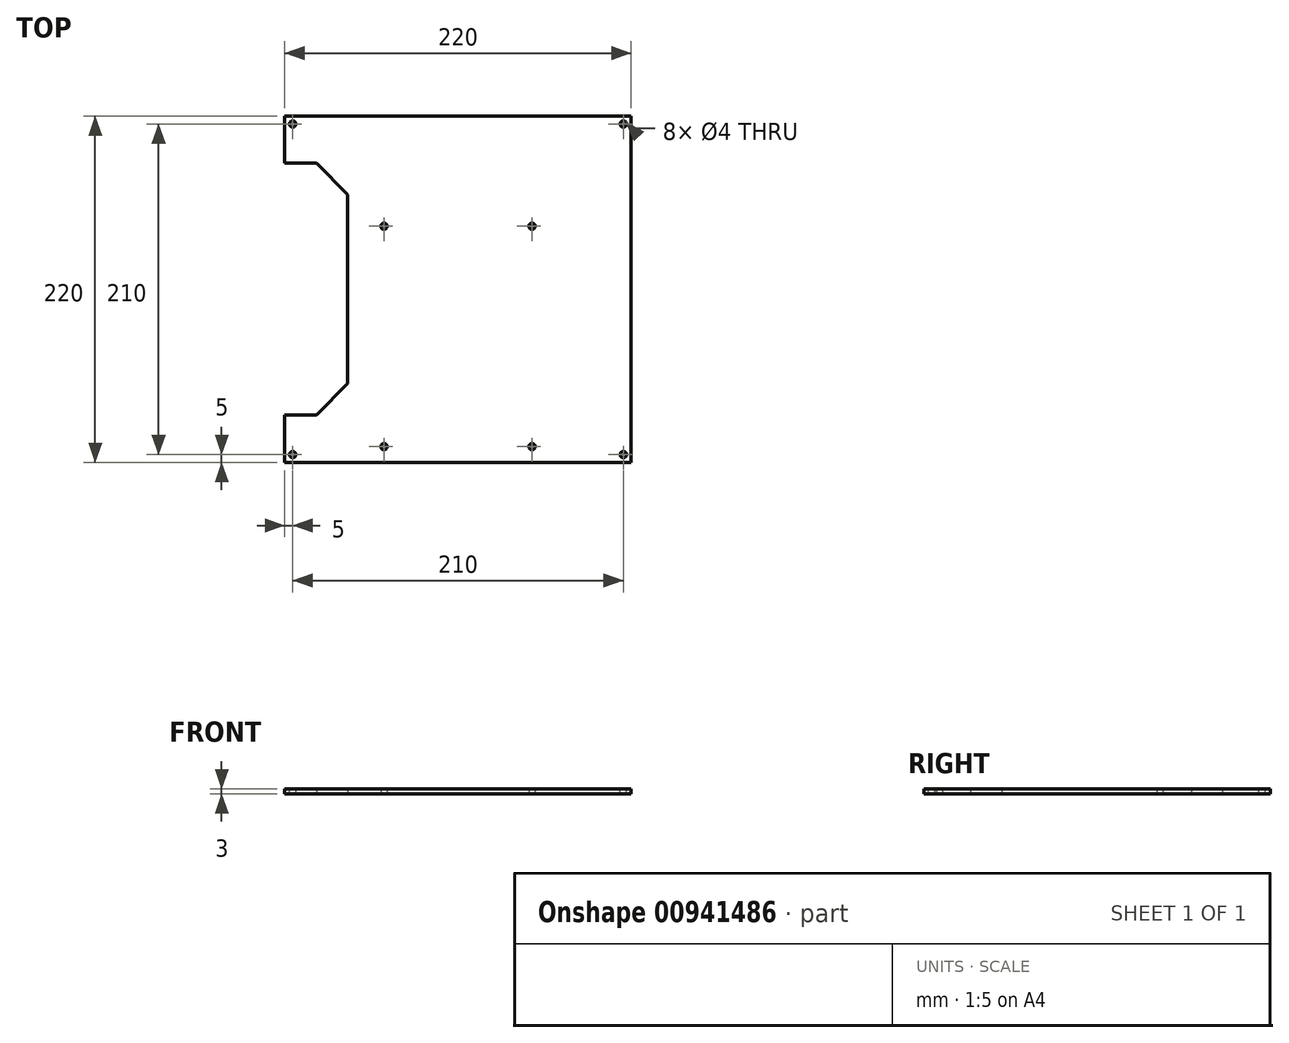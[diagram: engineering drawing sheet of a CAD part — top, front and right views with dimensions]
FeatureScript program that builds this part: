
annotation { "Feature Type Name" : "Feature", "Feature Type Description" : "" }
export const myFeature = defineFeature(function(context is Context, id is Id, definition is map)
    precondition{}
    {
        {
            var Q0;
            Q0=qCreatedBy(makeId("Top.planeOp"),FACE);
            var sketch = newSketch(context, id + "F0", { "sketchPlane" : qUnion([Q0])});
            skLineSegment(sketch, "E0.bottom", {"start": v(110, -110) * mm, "end": v(-110, -110) * mm});
            skLineSegment(sketch, "E0.top", {"start": v(110, 110) * mm, "end": v(-110, 110) * mm});
            skLineSegment(sketch, "E0.left", {"start": v(110, -110) * mm, "end": v(110, 110) * mm});
            skLineSegment(sketch, "E0.right", {"start": v(-110, -110) * mm, "end": v(-110, 110) * mm});
            skPoint(sketch, "E0.middle", {"position": v(0, 0) * mm});
            skSolve(sketch);
        }
        {
            var Q0;
            Q0=makeQuery(id+"F0.imprint","IMPRINT",FACE,{"disambiguationData":[TD([[makeQuery(id+"F0.imprint","IMPRINT",EDGE,{"derivedFrom":sQuery(id+"F0.wireOp",EDGE,"E0.bottom")}),-1.0]])]});
            extrude(context, id + "F1", {"entities" : qUnion([Q0]), "depth" : 3 * mm, "offsetDistance" : 25 * mm});
        }
        {
            var Q0;
            Q0=makeQuery(id+"F1.opExtrude","CAP_FACE",FACE,{"disambiguationData":[OSD([sQuery(id+"F0.wireOp",EDGE,"E0.bottom"),sQuery(id+"F0.wireOp",EDGE,"E0.top"),sQuery(id+"F0.wireOp",EDGE,"E0.left"),sQuery(id+"F0.wireOp",EDGE,"E0.right")])],"isStart":false});
            var sketch = newSketch(context, id + "F2", { "sketchPlane" : qUnion([Q0])});
            skCircle(sketch, "E1", {"center": v(-105, 105) * mm, "radius": 2 * mm});
            skCircle(sketch, "E2", {"center": v(105, 105) * mm, "radius": 2 * mm});
            skCircle(sketch, "E3", {"center": v(105, -105) * mm, "radius": 2 * mm});
            skCircle(sketch, "E4", {"center": v(-105, -105) * mm, "radius": 2 * mm});
            skLineSegment(sketch, "E5.bottom", {"start": v(-70, -80) * mm, "end": v(-150, -80) * mm});
            skLineSegment(sketch, "E5.top", {"start": v(-70, 80) * mm, "end": v(-150, 80) * mm});
            skLineSegment(sketch, "E5.left", {"start": v(-70, -80) * mm, "end": v(-70, 80) * mm});
            skLineSegment(sketch, "E5.right", {"start": v(-150, -80) * mm, "end": v(-150, 80) * mm});
            skPoint(sketch, "E5.middle", {"position": v(-110, 0) * mm});
            skSolve(sketch);
        }
        {
            var Q0;
            {var subQ0=sQuery(id+"F2.wireOp",EDGE,"E5.left");Q0=makeQuery(id+"F2.imprint","IMPRINT",FACE,{"disambiguationData":[TD([[makeQuery(id+"F2.imprint","IMPRINT",EDGE,{"derivedFrom":subQ0}),1.0]])]});}
            var Q1;
            Q1=makeQuery(id+"F2.imprint","IMPRINT",FACE,{"disambiguationData":[TD([[makeQuery(id+"F2.imprint","IMPRINT",EDGE,{"derivedFrom":sQuery(id+"F2.wireOp",EDGE,"E2")}),1.0]])]});
            var Q2;
            Q2=makeQuery(id+"F2.imprint","IMPRINT",FACE,{"disambiguationData":[TD([[makeQuery(id+"F2.imprint","IMPRINT",EDGE,{"derivedFrom":sQuery(id+"F2.wireOp",EDGE,"E3")}),1.0]])]});
            var Q3;
            Q3=makeQuery(id+"F2.imprint","IMPRINT",FACE,{"disambiguationData":[TD([[makeQuery(id+"F2.imprint","IMPRINT",EDGE,{"derivedFrom":sQuery(id+"F2.wireOp",EDGE,"E1")}),1.0]])]});
            var Q4;
            Q4=makeQuery(id+"F2.imprint","IMPRINT",FACE,{"disambiguationData":[TD([[makeQuery(id+"F2.imprint","IMPRINT",EDGE,{"derivedFrom":sQuery(id+"F2.wireOp",EDGE,"E4")}),1.0]])]});
            extrude(context, id + "F3", {"entities" : qUnion([Q0, Q1, Q2, Q3, Q4]), "operationType" : NewBodyOperationType.REMOVE, "oppositeDirection" : true, "depth" : 25 * mm, "offsetDistance" : 25 * mm});
        }
        {
            var Q0;
            Q0=makeQuery(id+"F3.boolean.opBoolean","COPY",EDGE,{"derivedFrom":makeQuery(id+"F3.opExtrude","SWEPT_EDGE",EDGE,{"disambiguationData":[OSD([sQuery(id+"F0.wireOp",EDGE,"E0.right"),sQuery(id+"F2.wireOp",EDGE,"E5.top")])]})});
            var Q1;
            Q1=makeQuery(id+"F3.boolean.opBoolean","COPY",EDGE,{"derivedFrom":makeQuery(id+"F3.opExtrude","SWEPT_EDGE",EDGE,{"disambiguationData":[OSD([sQuery(id+"F0.wireOp",EDGE,"E0.right"),sQuery(id+"F2.wireOp",EDGE,"E5.bottom")])]})});
            var Q2;
            Q2=makeQuery(id+"F3.boolean.opBoolean","COPY",EDGE,{"derivedFrom":makeQuery(id+"F3.opExtrude","SWEPT_EDGE",EDGE,{"disambiguationData":[OSD([sQuery(id+"F2.wireOp",EDGE,"E5.bottom"),sQuery(id+"F2.wireOp",EDGE,"E5.left")])]})});
            var Q3;
            Q3=makeQuery(id+"F3.boolean.opBoolean","COPY",EDGE,{"derivedFrom":makeQuery(id+"F3.opExtrude","SWEPT_EDGE",EDGE,{"disambiguationData":[OSD([sQuery(id+"F2.wireOp",EDGE,"E5.top"),sQuery(id+"F2.wireOp",EDGE,"E5.left")])]})});
            chamfer(context, id + "F4", {"entities" : qUnion([Q0, Q1, Q2, Q3]), "width" : 20 * mm, "tangentPropagation" : true});
        }
        {
            var Q0;
            Q0=makeQuery(id+"F1.opExtrude","CAP_FACE",FACE,{"disambiguationData":[OSD([sQuery(id+"F0.wireOp",EDGE,"E0.bottom"),sQuery(id+"F0.wireOp",EDGE,"E0.top"),sQuery(id+"F0.wireOp",EDGE,"E0.left"),sQuery(id+"F0.wireOp",EDGE,"E0.right")])],"isStart":true});
            var sketch = newSketch(context, id + "F5", { "sketchPlane" : qUnion([Q0])});
            skCircle(sketch, "E6", {"center": v(-47, -40) * mm, "radius": 2 * mm});
            skCircle(sketch, "E7", {"center": v(-47, 100) * mm, "radius": 2 * mm});
            skCircle(sketch, "E8", {"center": v(47, 100) * mm, "radius": 2 * mm});
            skCircle(sketch, "E9", {"center": v(47, -40) * mm, "radius": 2 * mm});
            skSolve(sketch);
        }
        {
            var Q0;
            Q0=makeQuery(id+"F5.imprint","IMPRINT",FACE,{"disambiguationData":[TD([[makeQuery(id+"F5.imprint","IMPRINT",EDGE,{"derivedFrom":sQuery(id+"F5.wireOp",EDGE,"E7")}),1.0]])]});
            var Q1;
            Q1=makeQuery(id+"F5.imprint","IMPRINT",FACE,{"disambiguationData":[TD([[makeQuery(id+"F5.imprint","IMPRINT",EDGE,{"derivedFrom":sQuery(id+"F5.wireOp",EDGE,"E6")}),1.0]])]});
            var Q2;
            Q2=makeQuery(id+"F5.imprint","IMPRINT",FACE,{"disambiguationData":[TD([[makeQuery(id+"F5.imprint","IMPRINT",EDGE,{"derivedFrom":sQuery(id+"F5.wireOp",EDGE,"E9")}),1.0]])]});
            var Q3;
            Q3=makeQuery(id+"F5.imprint","IMPRINT",FACE,{"disambiguationData":[TD([[makeQuery(id+"F5.imprint","IMPRINT",EDGE,{"derivedFrom":sQuery(id+"F5.wireOp",EDGE,"E8")}),1.0]])]});
            extrude(context, id + "F6", {"entities" : qUnion([Q0, Q1, Q2, Q3]), "operationType" : NewBodyOperationType.REMOVE, "oppositeDirection" : true, "depth" : 25 * mm, "offsetDistance" : 25 * mm});
        }
    });
